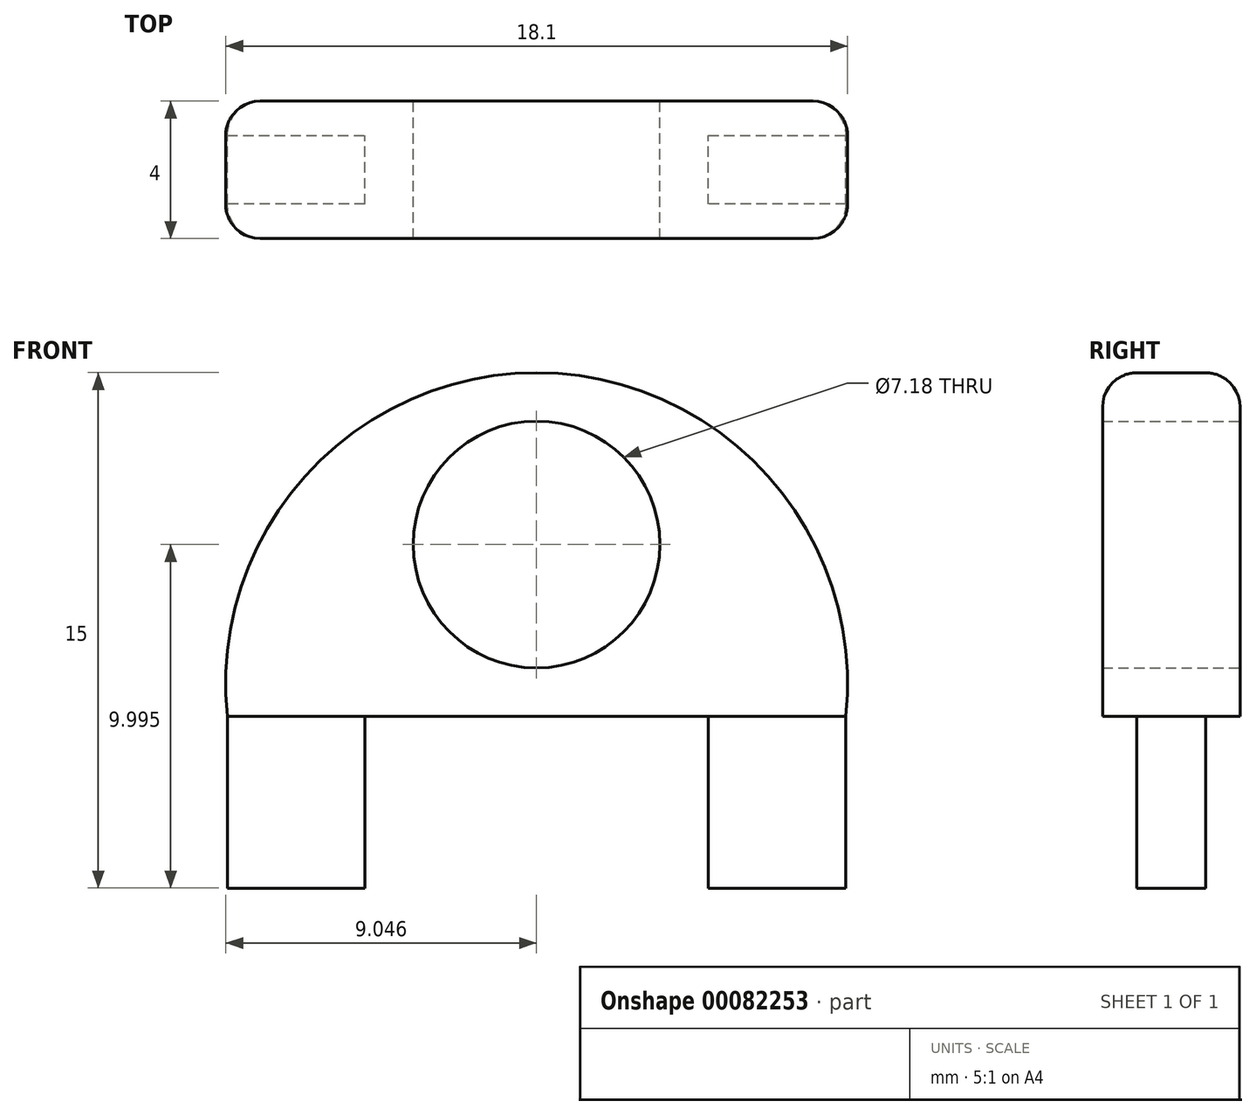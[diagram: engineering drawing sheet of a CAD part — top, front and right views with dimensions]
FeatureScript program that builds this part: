
annotation { "Feature Type Name" : "Feature", "Feature Type Description" : "" }
export const myFeature = defineFeature(function(context is Context, id is Id, definition is map)
    precondition{}
    {
        {
            var Q0;
            Q0=qCreatedBy(makeId("Front.planeOp"),FACE);
            var sketch = newSketch(context, id + "F0", { "sketchPlane" : qUnion([Q0])});
            skLineSegment(sketch, "E0", {"start": v(-28.82, 17.72) * mm, "end": v(-18.82, 17.72) * mm});
            skLineSegment(sketch, "E1", {"start": v(-28.82, 17.72) * mm, "end": v(-28.82, 12.72) * mm});
            skLineSegment(sketch, "E2", {"start": v(-18.82, 17.72) * mm, "end": v(-18.82, 12.72) * mm});
            skLineSegment(sketch, "E3", {"start": v(-18.82, 12.72) * mm, "end": v(-14.82, 12.72) * mm});
            skLineSegment(sketch, "E4", {"start": v(-28.82, 12.72) * mm, "end": v(-32.82, 12.72) * mm});
            skLineSegment(sketch, "E5", {"start": v(-32.82, 12.72) * mm, "end": v(-32.82, 17.72) * mm});
            skLineSegment(sketch, "E6", {"start": v(-14.82, 12.72) * mm, "end": v(-14.82, 17.72) * mm});
            skArc(sketch, "E7", {"start": v(-14.82, 17.72) * mm, "mid": v(-23.82, 27.72) * mm, "end": v(-32.82, 17.72) * mm});
            skCircle(sketch, "E8", {"center": v(-23.82, 22.72) * mm, "radius": 3.59 * mm});
            skSolve(sketch);
        }
        {
            var Q0;
            Q0 = qSketchRegion(id + "F0", true);
            extrude(context, id + "F1", {"entities" : qUnion([Q0]), "depth" : 2 * mm});
        }
        {
            var Q0;
            Q0=makeQuery(id+"F1.opExtrude","CAP_FACE",FACE,{"disambiguationData":[OSD([sQuery(id+"F0.wireOp",EDGE,"E0"),sQuery(id+"F0.wireOp",EDGE,"E1"),sQuery(id+"F0.wireOp",EDGE,"E2"),sQuery(id+"F0.wireOp",EDGE,"E3"),sQuery(id+"F0.wireOp",EDGE,"E4"),sQuery(id+"F0.wireOp",EDGE,"E5"),sQuery(id+"F0.wireOp",EDGE,"E6"),sQuery(id+"F0.wireOp",EDGE,"E7"),sQuery(id+"F0.wireOp",EDGE,"E8")])],"isStart":false});
            var sketch = newSketch(context, id + "F2", { "sketchPlane" : qUnion([Q0])});
            skLineSegment(sketch, "E9", {"start": v(-28.82, 17.72) * mm, "end": v(-32.82, 17.72) * mm});
            skLineSegment(sketch, "E10", {"start": v(-18.82, 17.72) * mm, "end": v(-14.82, 17.72) * mm});
            skSolve(sketch);
        }
        {
            var Q0;
            Q0=makeQuery(id+"F2.imprint","IMPRINT",FACE,{"disambiguationData":[TD([[makeQuery(id+"F2.imprint","IMPRINT",EDGE,{"derivedFrom":sQuery(id+"F2.wireOp",EDGE,"E9")}),-1.0]])]});
            extrude(context, id + "F3", {"entities" : qUnion([Q0]), "operationType" : NewBodyOperationType.ADD, "depth" : 1 * mm});
        }
        {
            var Q0;
            Q0=makeQuery(id+"F1.opExtrude","CAP_FACE",FACE,{"disambiguationData":[OSD([sQuery(id+"F0.wireOp",EDGE,"E0"),sQuery(id+"F0.wireOp",EDGE,"E1"),sQuery(id+"F0.wireOp",EDGE,"E2"),sQuery(id+"F0.wireOp",EDGE,"E3"),sQuery(id+"F0.wireOp",EDGE,"E4"),sQuery(id+"F0.wireOp",EDGE,"E5"),sQuery(id+"F0.wireOp",EDGE,"E6"),sQuery(id+"F0.wireOp",EDGE,"E7"),sQuery(id+"F0.wireOp",EDGE,"E8")])],"isStart":true});
            var sketch = newSketch(context, id + "F4", { "sketchPlane" : qUnion([Q0])});
            skLineSegment(sketch, "E11", {"start": v(18.82, 17.72) * mm, "end": v(14.82, 17.72) * mm});
            skLineSegment(sketch, "E12", {"start": v(28.82, 17.72) * mm, "end": v(32.82, 17.72) * mm});
            skSolve(sketch);
        }
        {
            var Q0;
            Q0 = qSketchRegion(id + "F4", true);
            var Q1;
            Q1=makeQuery(id+"F4.imprint","IMPRINT",FACE,{"disambiguationData":[TD([[makeQuery(id+"F4.imprint","IMPRINT",EDGE,{"derivedFrom":sQuery(id+"F4.wireOp",EDGE,"E11")}),-1.0]])]});
            extrude(context, id + "F5", {"entities" : qUnion([Q0, Q1]), "operationType" : NewBodyOperationType.ADD, "depth" : 1 * mm});
        }
        {
            var Q0;
            Q0=makeQuery(id+"F5.opExtrude","CAP_EDGE",EDGE,{"disambiguationData":[OSD([sQuery(id+"F0.wireOp",EDGE,"E7")])],"isStart":false});
            fillet(context, id + "F6", {"entities" : qUnion([Q0]), "radius" : 1 * mm, "tangentPropagation" : true, "allowEdgeOverflow" : false});
        }
        {
            var Q0;
            Q0=makeQuery(id+"F3.opExtrude","CAP_EDGE",EDGE,{"disambiguationData":[OSD([sQuery(id+"F0.wireOp",EDGE,"E7")])],"isStart":false});
            fillet(context, id + "F7", {"entities" : qUnion([Q0]), "radius" : 1 * mm, "tangentPropagation" : true, "allowEdgeOverflow" : false});
        }
    });
